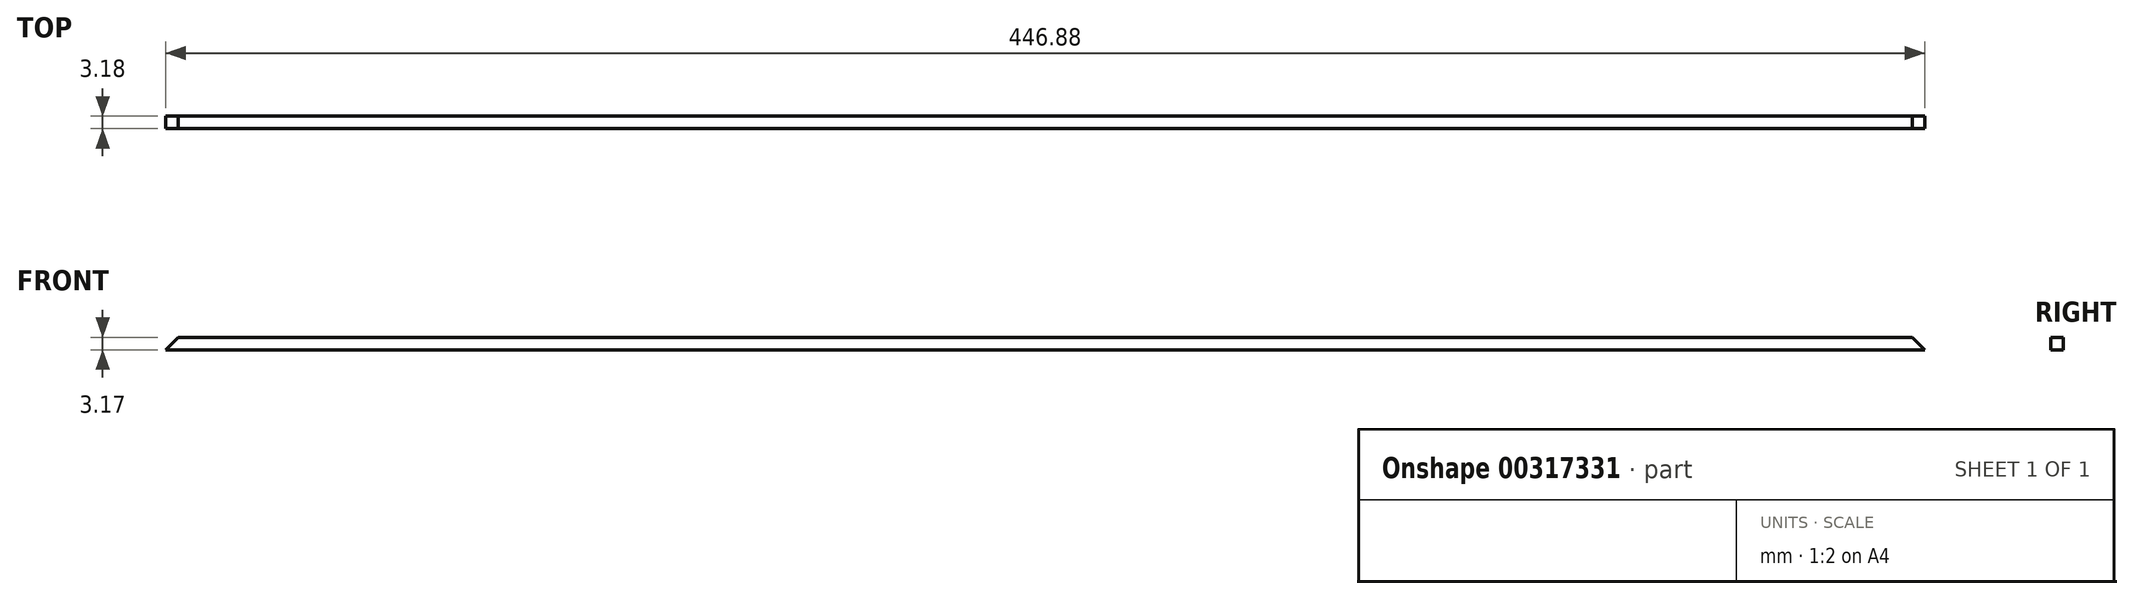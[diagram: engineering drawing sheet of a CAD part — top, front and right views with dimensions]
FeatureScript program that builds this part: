
annotation { "Feature Type Name" : "Feature", "Feature Type Description" : "" }
export const myFeature = defineFeature(function(context is Context, id is Id, definition is map)
    precondition{}
    {
        {
            var Q0;
            Q0=qCreatedBy(makeId("Front.planeOp"),FACE);
            var sketch = newSketch(context, id + "F0", { "sketchPlane" : qUnion([Q0])});
            skLineSegment(sketch, "E0", {"start": v(-220.27, 3.18) * mm, "end": v(220.27, 3.18) * mm});
            skLineSegment(sketch, "E1", {"start": v(-223.44, 0) * mm, "end": v(223.44, 0) * mm});
            skLineSegment(sketch, "E2", {"start": v(-223.44, 0) * mm, "end": v(-220.27, 3.18) * mm});
            skLineSegment(sketch, "E3", {"start": v(220.27, 3.18) * mm, "end": v(223.44, 0) * mm});
            skSolve(sketch);
        }
        {
            var Q0;
            Q0=makeQuery(id+"F0.imprint","IMPRINT",FACE,{"disambiguationData":[TD([[makeQuery(id+"F0.imprint","IMPRINT",EDGE,{"derivedFrom":sQuery(id+"F0.wireOp",EDGE,"E0")}),-1.0]])]});
            extrude(context, id + "F1", {"entities" : qUnion([Q0]), "endBound" : BoundingType.SYMMETRIC, "depth" : 3.17 * mm});
        }
    });
